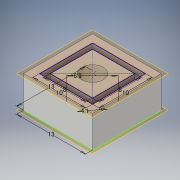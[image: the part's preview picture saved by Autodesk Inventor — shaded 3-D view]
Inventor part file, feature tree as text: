
AUTODESK INVENTOR PART (.ipt)
format: ipt  version: 2019.3 (Build 233278000, 278)  size: 134,144 bytes
history: native  units: in
note: dims shown in document units (in); Inventor stores cm internally (conversion verified against a paired STEP export)
features: extrude x4, sketch x2, other x1
ambient origin geometry x8: Origin, YZ Plane, XZ Plane, XY Plane, X Axis, Y Axis, Z Axis, Center Point
bodies: Body1 (feature_tree)
feature tree (7):
  other  "作業平面2"
  sketch  "スケッチ3"
  sketch  "スケッチ1"
  extrude  "押し出し8"  Depth=0.2362in
  extrude  "押し出し9"  Depth=0.315in
  extrude  "押し出し10"  Depth=0.315in
  extrude  "押し出し11"  Depth=0.3937in
